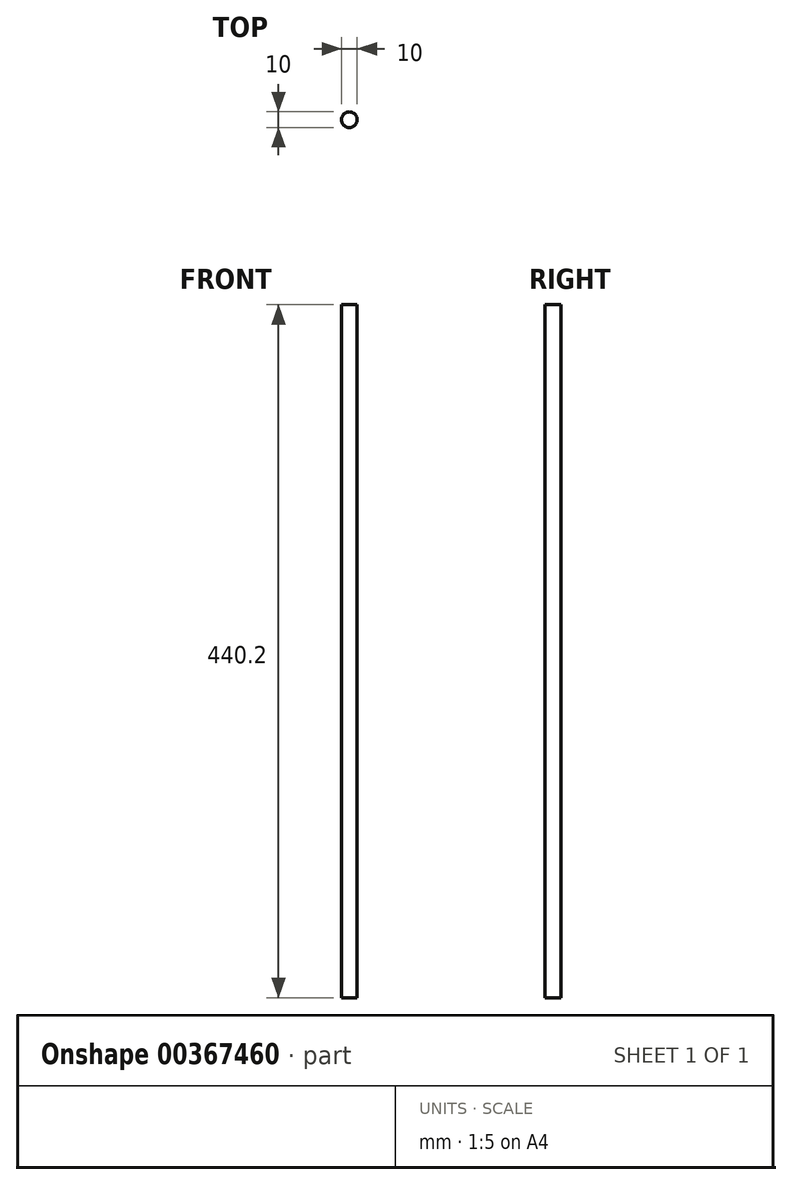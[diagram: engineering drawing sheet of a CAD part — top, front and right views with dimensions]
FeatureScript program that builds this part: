
annotation { "Feature Type Name" : "Feature", "Feature Type Description" : "" }
export const myFeature = defineFeature(function(context is Context, id is Id, definition is map)
    precondition{}
    {
        {
            var Q0;
            Q0=qCreatedBy(makeId("Top.planeOp"),FACE);
            var sketch = newSketch(context, id + "F0", { "sketchPlane" : qUnion([Q0])});
            skCircle(sketch, "E0", {"center": v(0, 0) * mm, "radius": 5 * mm});
            skSolve(sketch);
        }
        {
            var Q0;
            Q0=qSketchRegion(id+"F0",true);
            extrude(context, id + "F1", {"entities" : qUnion([Q0]), "depth" : 440.2 * mm});
        }
    });
